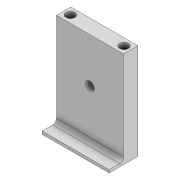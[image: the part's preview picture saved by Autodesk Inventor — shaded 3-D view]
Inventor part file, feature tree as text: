
AUTODESK INVENTOR PART (.ipt)
format: ipt  version: 2022 (Build 260153000, 153)  size: 123,392 bytes
history: native  units: mm
features: extrude x4, sketch x4, fillet x1, projected_geometry x1
ambient origin geometry x8: Origin, YZ Plane, XZ Plane, XY Plane, X Axis, Y Axis, Z Axis, Center Point
bodies: Solid1 (feature_tree)
feature tree (10):
  extrude  "Extrusion1"  Depth=100.0mm
  extrude  "Extrusion3"  Depth=15.0mm
  extrude  "Extrusion4"  Depth=70.0mm
  fillet  "Fillet1"  Radius=70.0mm
  extrude  "Extrusion5"  Depth=15.0mm TaperAngle=0.0deg
  sketch  "Sketch1"  dims[d0=70.0mm d1=100.0mm]
  sketch  "Sketch3"  dims[d2=15.0mm d3=0.0mm d7=9.3mm]
  sketch  "Sketch4"  dims[d8=9.3mm d9=56.0mm d10=70.0mm]
  sketch  "Sketch5"  dims[d11=7.0mm d12=15.0mm d13=0.0mm d14=3.0mm d15=15.0mm d16=0.0mm d17=4.0mm d18=9.25mm d21=11.0mm d22=-0.349066mm]
  projected_geometry  "Projected Loop1"
